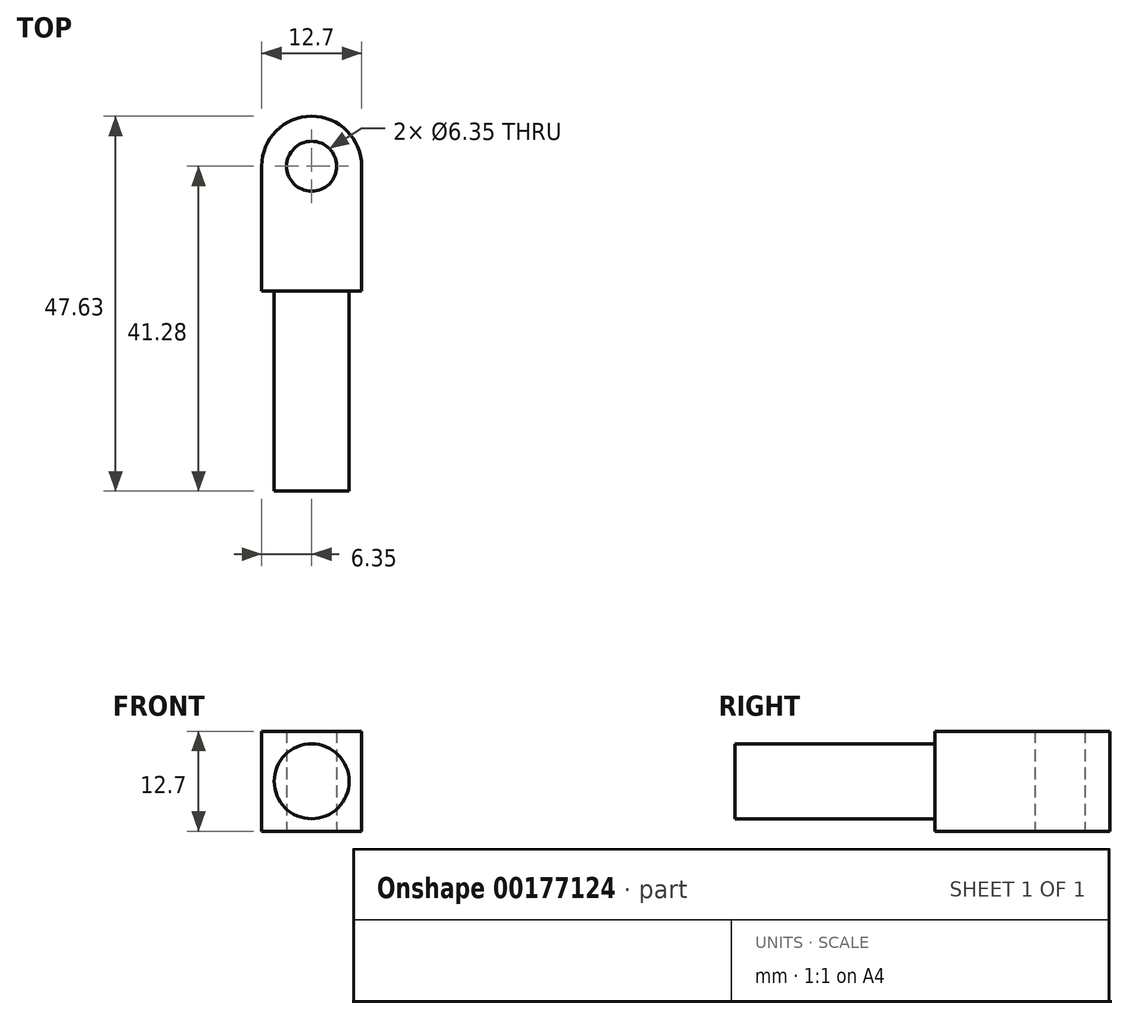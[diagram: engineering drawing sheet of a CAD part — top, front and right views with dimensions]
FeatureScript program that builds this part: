
annotation { "Feature Type Name" : "Feature", "Feature Type Description" : "" }
export const myFeature = defineFeature(function(context is Context, id is Id, definition is map)
    precondition{}
    {
        {
            var Q0;
            Q0=qCreatedBy(makeId("Top.planeOp"),FACE);
            var sketch = newSketch(context, id + "F0", { "sketchPlane" : qUnion([Q0])});
            skArc(sketch, "E0", {"start": v(6.35, 0) * mm, "mid": v(0, 6.35) * mm, "end": v(-6.35, 0) * mm});
            skLineSegment(sketch, "E1.top", {"start": v(-6.35, -15.88) * mm, "end": v(6.35, -15.88) * mm});
            skLineSegment(sketch, "E1.left", {"start": v(-6.35, 0) * mm, "end": v(-6.35, -15.88) * mm});
            skLineSegment(sketch, "E1.right", {"start": v(6.35, 0) * mm, "end": v(6.35, -15.88) * mm});
            skCircle(sketch, "E2", {"center": v(0, 0) * mm, "radius": 3.18 * mm});
            skSolve(sketch);
        }
        {
            var Q0;
            Q0 = qSketchRegion(id + "F0", true);
            extrude(context, id + "F1", {"entities" : qUnion([Q0]), "endBound" : BoundingType.SYMMETRIC, "depth" : 12.7 * mm});
        }
        {
            var Q0;
            Q0=makeQuery(id+"F1.opExtrude","SWEPT_FACE",FACE,{"disambiguationData":[OSD([sQuery(id+"F0.wireOp",EDGE,"E1.top")])]});
            var sketch = newSketch(context, id + "F2", { "sketchPlane" : qUnion([Q0])});
            skCircle(sketch, "E3", {"center": v(0, 0) * mm, "radius": 4.76 * mm});
            skSolve(sketch);
        }
        {
            var Q0;
            Q0 = qSketchRegion(id + "F2", true);
            extrude(context, id + "F3", {"entities" : qUnion([Q0]), "operationType" : NewBodyOperationType.ADD, "depth" : 25.4 * mm});
        }
        {
            var Q0;
            Q0=makeQuery(id+"F1.opExtrude","SWEPT_BODY",BODY,{"disambiguationData":[OSD([sQuery(id+"F0.wireOp",EDGE,"E0"),sQuery(id+"F0.wireOp",EDGE,"E1.top"),sQuery(id+"F0.wireOp",EDGE,"E1.left"),sQuery(id+"F0.wireOp",EDGE,"E1.right"),sQuery(id+"F0.wireOp",EDGE,"E2")])]});
            transform(context, id + "F4", {"entities" : qUnion([Q0]), "transformType" : TransformType.TRANSLATION_3D, "dx" : 0 * mm, "dy" : 0 * mm, "dz" : 0 * mm, "makeCopy" : true});
        }
    });
